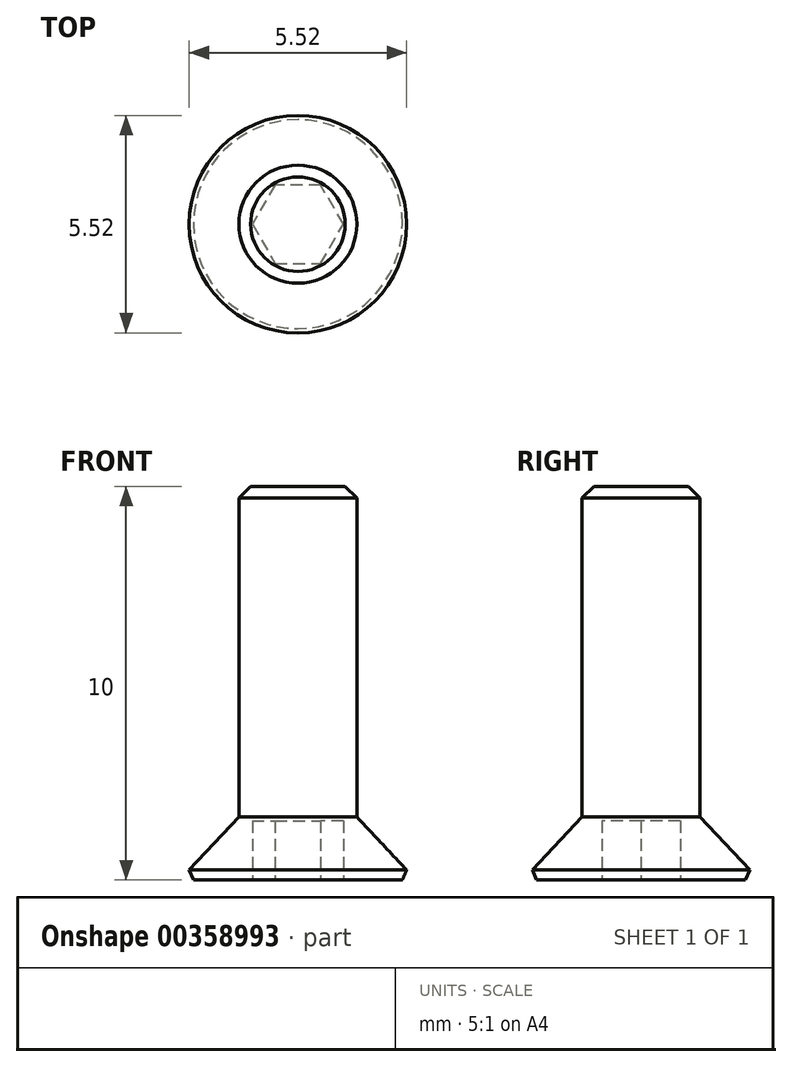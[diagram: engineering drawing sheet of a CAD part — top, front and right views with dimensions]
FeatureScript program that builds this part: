
annotation { "Feature Type Name" : "Feature", "Feature Type Description" : "" }
export const myFeature = defineFeature(function(context is Context, id is Id, definition is map)
    precondition{}
    {
        {
            assignVariable(context, id + "F0", {"name" : "d", "anyValue" : 3});
        }
        {
            var Q0;
            Q0=qCreatedBy(makeId("Front.planeOp"),FACE);
            var sketch = newSketch(context, id + "F1", { "sketchPlane" : qUnion([Q0])});
            skLineSegment(sketch, "E0", {"start": v(0, 0) * mm, "end": v(3, 0) * mm});
            skLineSegment(sketch, "E1", {"start": v(3, 0) * mm, "end": v(1.5, 1.6) * mm});
            skLineSegment(sketch, "E2", {"start": v(1.5, 1.6) * mm, "end": v(1.5, 10) * mm});
            skLineSegment(sketch, "E3", {"start": v(1.5, 10) * mm, "end": v(0, 10) * mm});
            skLineSegment(sketch, "E4", {"start": v(0, 10) * mm, "end": v(0, 0) * mm});
            skSolve(sketch);
        }
        {
            var Q0;
            Q0 = qSketchRegion(id + "F1", true);
            var Q1;
            Q1=sQuery(id+"F1.wireOp",EDGE,"E4");
            revolve(context, id + "F2", {"entities" : qUnion([Q0]), "axis" : qUnion([Q1]), "revolveType" : RevolveType.FULL});
        }
        {
            var Q0;
            Q0=makeQuery(id+"F2.opRevolve","SWEPT_FACE",FACE,{"disambiguationData":[OSD([sQuery(id+"F1.wireOp",EDGE,"E0")])]});
            var sketch = newSketch(context, id + "F3", { "sketchPlane" : qUnion([Q0])});
            skCircle(sketch, "E5.cCircle", {"center": v(0, 0) * mm, "radius": 1 * mm, "construction": true});
            skLineSegment(sketch, "E5.0", {"start": v(-0.58, 1) * mm, "end": v(0.58, 1) * mm});
            skLineSegment(sketch, "E5.1", {"start": v(0.58, 1) * mm, "end": v(1.15, 0) * mm});
            skLineSegment(sketch, "E5.2", {"start": v(1.15, 0) * mm, "end": v(0.58, -1) * mm});
            skLineSegment(sketch, "E5.3", {"start": v(0.58, -1) * mm, "end": v(-0.58, -1) * mm});
            skLineSegment(sketch, "E5.4", {"start": v(-0.58, -1) * mm, "end": v(-1.15, 0) * mm});
            skLineSegment(sketch, "E5.5", {"start": v(-1.15, 0) * mm, "end": v(-0.58, 1) * mm});
            skPoint(sketch, "E5.0.midPoint", {"position": v(0, 1) * mm});
            skSolve(sketch);
        }
        {
            var Q0;
            Q0 = qSketchRegion(id + "F3", true);
            extrude(context, id + "F4", {"entities" : qUnion([Q0]), "operationType" : NewBodyOperationType.REMOVE, "oppositeDirection" : true, "depth" : (getVariable(context, 'd') / 2) * mm});
        }
        {
            var Q0;
            Q0=makeQuery(id+"F2.opRevolve","SWEPT_EDGE",EDGE,{"disambiguationData":[OSD([sQuery(id+"F1.wireOp",EDGE,"E0"),sQuery(id+"F1.wireOp",EDGE,"E1")])]});
            var Q1;
            Q1=makeQuery(id+"F4.boolean.opBoolean","COPY",EDGE,{"derivedFrom":makeQuery(id+"F4.opExtrude","CAP_EDGE",EDGE,{"disambiguationData":[OSD([sQuery(id+"F3.wireOp",EDGE,"E5.0")])],"isStart":true})});
            var Q2;
            Q2=makeQuery(id+"F4.boolean.opBoolean","COPY",EDGE,{"derivedFrom":makeQuery(id+"F4.opExtrude","CAP_EDGE",EDGE,{"disambiguationData":[OSD([sQuery(id+"F3.wireOp",EDGE,"E5.5")])],"isStart":true})});
            var Q3;
            Q3=makeQuery(id+"F4.boolean.opBoolean","COPY",EDGE,{"derivedFrom":makeQuery(id+"F4.opExtrude","CAP_EDGE",EDGE,{"disambiguationData":[OSD([sQuery(id+"F3.wireOp",EDGE,"E5.4")])],"isStart":true})});
            var Q4;
            Q4=makeQuery(id+"F4.boolean.opBoolean","COPY",EDGE,{"derivedFrom":makeQuery(id+"F4.opExtrude","CAP_EDGE",EDGE,{"disambiguationData":[OSD([sQuery(id+"F3.wireOp",EDGE,"E5.3")])],"isStart":true})});
            var Q5;
            Q5=makeQuery(id+"F4.boolean.opBoolean","COPY",EDGE,{"derivedFrom":makeQuery(id+"F4.opExtrude","CAP_EDGE",EDGE,{"disambiguationData":[OSD([sQuery(id+"F3.wireOp",EDGE,"E5.2")])],"isStart":true})});
            var Q6;
            Q6=makeQuery(id+"F4.boolean.opBoolean","COPY",EDGE,{"derivedFrom":makeQuery(id+"F4.opExtrude","CAP_EDGE",EDGE,{"disambiguationData":[OSD([sQuery(id+"F3.wireOp",EDGE,"E5.1")])],"isStart":true})});
            chamfer(context, id + "F5", {"entities" : qUnion([Q0, Q1, Q2, Q3, Q4, Q5, Q6]), "width" : (getVariable(context, 'd') / 20) * mm, "tangentPropagation" : true});
        }
        {
            var Q0;
            Q0=makeQuery(id+"F2.opRevolve","SWEPT_EDGE",EDGE,{"disambiguationData":[OSD([sQuery(id+"F1.wireOp",EDGE,"E2"),sQuery(id+"F1.wireOp",EDGE,"E3")])]});
            chamfer(context, id + "F6", {"entities" : qUnion([Q0]), "width" : (getVariable(context, 'd') / 10) * mm, "tangentPropagation" : true});
        }
    });
